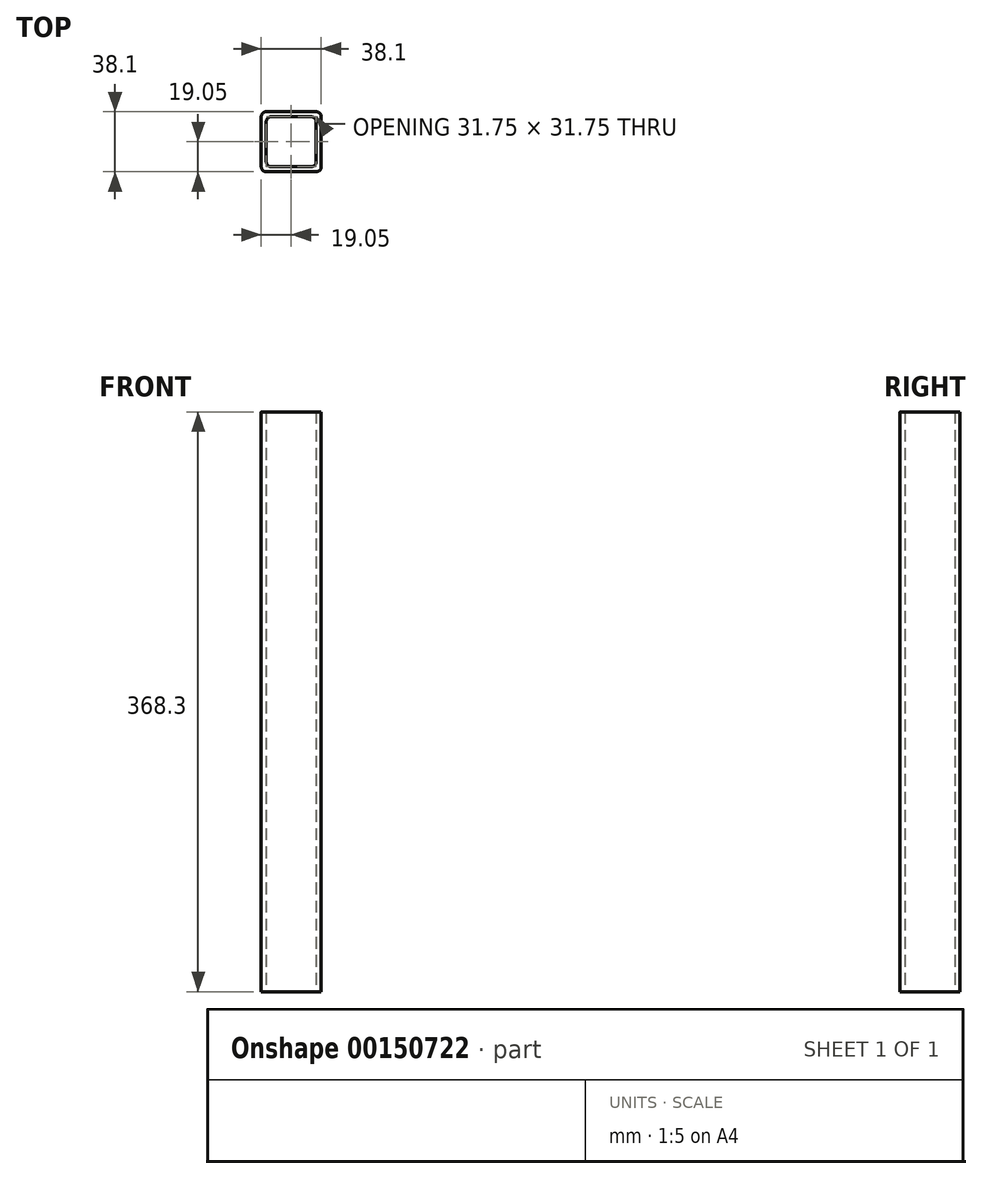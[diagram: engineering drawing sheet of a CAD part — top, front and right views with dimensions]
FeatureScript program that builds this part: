
annotation { "Feature Type Name" : "Feature", "Feature Type Description" : "" }
export const myFeature = defineFeature(function(context is Context, id is Id, definition is map)
    precondition{}
    {
        {
            var Q0;
            Q0=qCreatedBy(makeId("Top.planeOp"),FACE);
            var sketch = newSketch(context, id + "F0", { "sketchPlane" : qUnion([Q0])});
            skLineSegment(sketch, "E0.bottom", {"start": v(15.87, 19.05) * mm, "end": v(-15.87, 19.05) * mm});
            skLineSegment(sketch, "E0.top", {"start": v(15.88, -19.05) * mm, "end": v(-15.87, -19.05) * mm});
            skLineSegment(sketch, "E0.left", {"start": v(19.05, 15.87) * mm, "end": v(19.05, -15.87) * mm});
            skLineSegment(sketch, "E0.right", {"start": v(-19.05, 15.87) * mm, "end": v(-19.05, -15.87) * mm});
            skPoint(sketch, "E0.middle", {"position": v(0, 0) * mm});
            skPoint(sketch, "E1.visualSharp", {"position": v(-19.05, 19.05) * mm});
            skArc(sketch, "E1.filletArc", {"start": v(-15.87, 19.05) * mm, "mid": v(-18.12, 18.12) * mm, "end": v(-19.05, 15.87) * mm});
            skPoint(sketch, "E2.visualSharp", {"position": v(19.05, 19.05) * mm});
            skArc(sketch, "E2.filletArc", {"start": v(19.05, 15.87) * mm, "mid": v(18.12, 18.12) * mm, "end": v(15.87, 19.05) * mm});
            skPoint(sketch, "E3.visualSharp", {"position": v(-19.05, -19.05) * mm});
            skArc(sketch, "E3.filletArc", {"start": v(-19.05, -15.87) * mm, "mid": v(-18.12, -18.12) * mm, "end": v(-15.87, -19.05) * mm});
            skPoint(sketch, "E4.visualSharp", {"position": v(19.05, -19.05) * mm});
            skArc(sketch, "E4.filletArc", {"start": v(15.88, -19.05) * mm, "mid": v(18.12, -18.12) * mm, "end": v(19.05, -15.87) * mm});
            skLineSegment(sketch, "E5.bottom", {"start": v(12.7, 15.88) * mm, "end": v(-12.7, 15.88) * mm});
            skLineSegment(sketch, "E5.top", {"start": v(12.7, -15.88) * mm, "end": v(-12.7, -15.88) * mm});
            skLineSegment(sketch, "E5.left", {"start": v(15.87, 12.7) * mm, "end": v(15.88, -12.7) * mm});
            skLineSegment(sketch, "E5.right", {"start": v(-15.88, 12.7) * mm, "end": v(-15.87, -12.7) * mm});
            skPoint(sketch, "E6.visualSharp", {"position": v(-15.88, 15.87) * mm});
            skArc(sketch, "E6.filletArc", {"start": v(-12.7, 15.88) * mm, "mid": v(-14.95, 14.95) * mm, "end": v(-15.88, 12.7) * mm});
            skPoint(sketch, "E7.visualSharp", {"position": v(-15.87, -15.88) * mm});
            skArc(sketch, "E7.filletArc", {"start": v(-15.88, -12.7) * mm, "mid": v(-14.95, -14.95) * mm, "end": v(-12.7, -15.88) * mm});
            skArc(sketch, "E8.filletArc", {"start": v(12.7, -15.88) * mm, "mid": v(14.95, -14.95) * mm, "end": v(15.88, -12.7) * mm});
            skPoint(sketch, "E9.visualSharp", {"position": v(15.87, 15.88) * mm});
            skArc(sketch, "E9.filletArc", {"start": v(15.88, 12.7) * mm, "mid": v(14.95, 14.95) * mm, "end": v(12.7, 15.88) * mm});
            skSolve(sketch);
        }
        {
            var Q0;
            Q0 = qSketchRegion(id + "F0", true);
            extrude(context, id + "F1", {"entities" : qUnion([Q0]), "depth" : 368.3 * mm});
        }
    });
